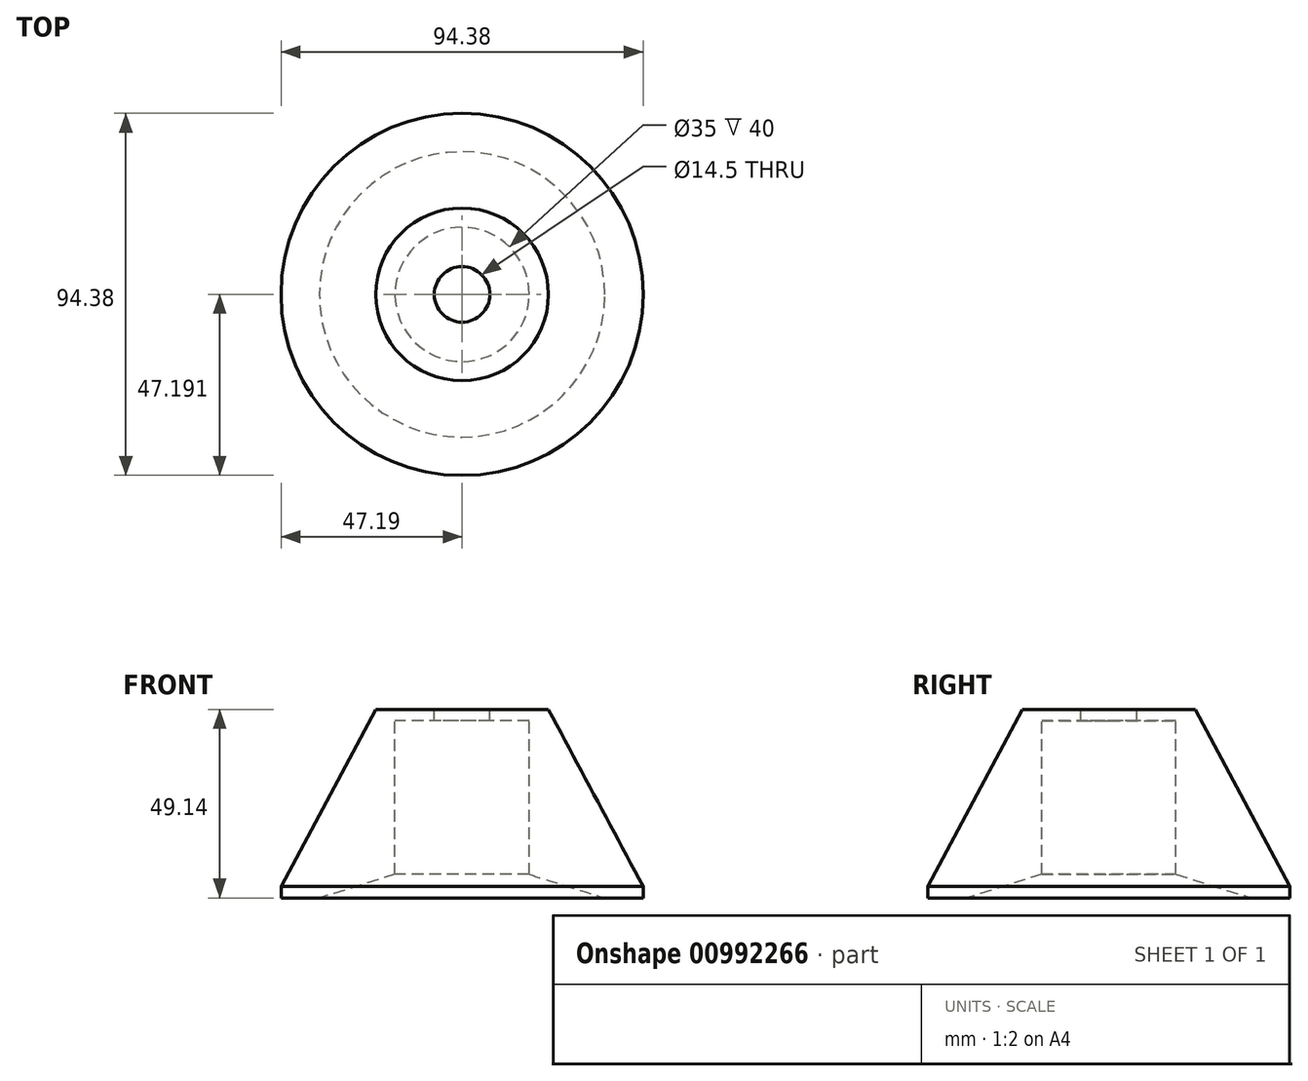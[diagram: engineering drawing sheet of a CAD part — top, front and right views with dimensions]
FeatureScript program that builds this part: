
annotation { "Feature Type Name" : "Feature", "Feature Type Description" : "" }
export const myFeature = defineFeature(function(context is Context, id is Id, definition is map)
    precondition{}
    {
        {
            var Q0;
            Q0=qCreatedBy(makeId("Right.planeOp"),FACE);
            var sketch = newSketch(context, id + "F0", { "sketchPlane" : qUnion([Q0])});
            skLineSegment(sketch, "E0", {"start": v(48.96, 82.66) * mm, "end": v(48.96, 79.66) * mm});
            skLineSegment(sketch, "E1", {"start": v(48.96, 79.66) * mm, "end": v(66.46, 79.66) * mm});
            skLineSegment(sketch, "E2", {"start": v(66.46, 79.66) * mm, "end": v(66.46, 39.66) * mm});
            skLineSegment(sketch, "E3", {"start": v(66.46, 39.66) * mm, "end": v(86.15, 33.52) * mm});
            skLineSegment(sketch, "E4", {"start": v(86.15, 33.52) * mm, "end": v(96.15, 33.52) * mm});
            skLineSegment(sketch, "E5", {"start": v(96.15, 33.52) * mm, "end": v(96.15, 36.52) * mm});
            skLineSegment(sketch, "E6", {"start": v(96.15, 36.52) * mm, "end": v(71.46, 82.66) * mm});
            skLineSegment(sketch, "E7", {"start": v(71.46, 82.66) * mm, "end": v(48.96, 82.66) * mm});
            skSolve(sketch);
        }
        {
            var Q0;
            Q0=makeQuery(id+"F0.imprint","IMPRINT",FACE,{"disambiguationData":[TD([[makeQuery(id+"F0.imprint","IMPRINT",EDGE,{"derivedFrom":sQuery(id+"F0.wireOp",EDGE,"E0")}),1.0]])]});
            var Q1;
            Q1=sQuery(id+"F0.wireOp",EDGE,"E0");
            revolve(context, id + "F1", {"surfaceOperationType" : NewSurfaceOperationType.NEW, "entities" : qUnion([Q0]), "axis" : qUnion([Q1]), "revolveType" : RevolveType.FULL});
        }
        {
            var Q0;
            Q0=makeQuery(id+"F1.opRevolve","SWEPT_FACE",FACE,{"disambiguationData":[OSD([sQuery(id+"F0.wireOp",EDGE,"E7")])]});
            var sketch = newSketch(context, id + "F2", { "sketchPlane" : qUnion([Q0])});
            skCircle(sketch, "E8", {"center": v(0, 48.96) * mm, "radius": 7.25 * mm});
            skSolve(sketch);
        }
        {
            var Q0;
            Q0 = qSketchRegion(id + "F2", true);
            extrude(context, id + "F3", {"entities" : qUnion([Q0]), "operationType" : NewBodyOperationType.REMOVE, "endBound" : BoundingType.THROUGH_ALL, "oppositeDirection" : true, "depth" : 25.4 * mm, "offsetDistance" : 25.4 * mm});
        }
    });
